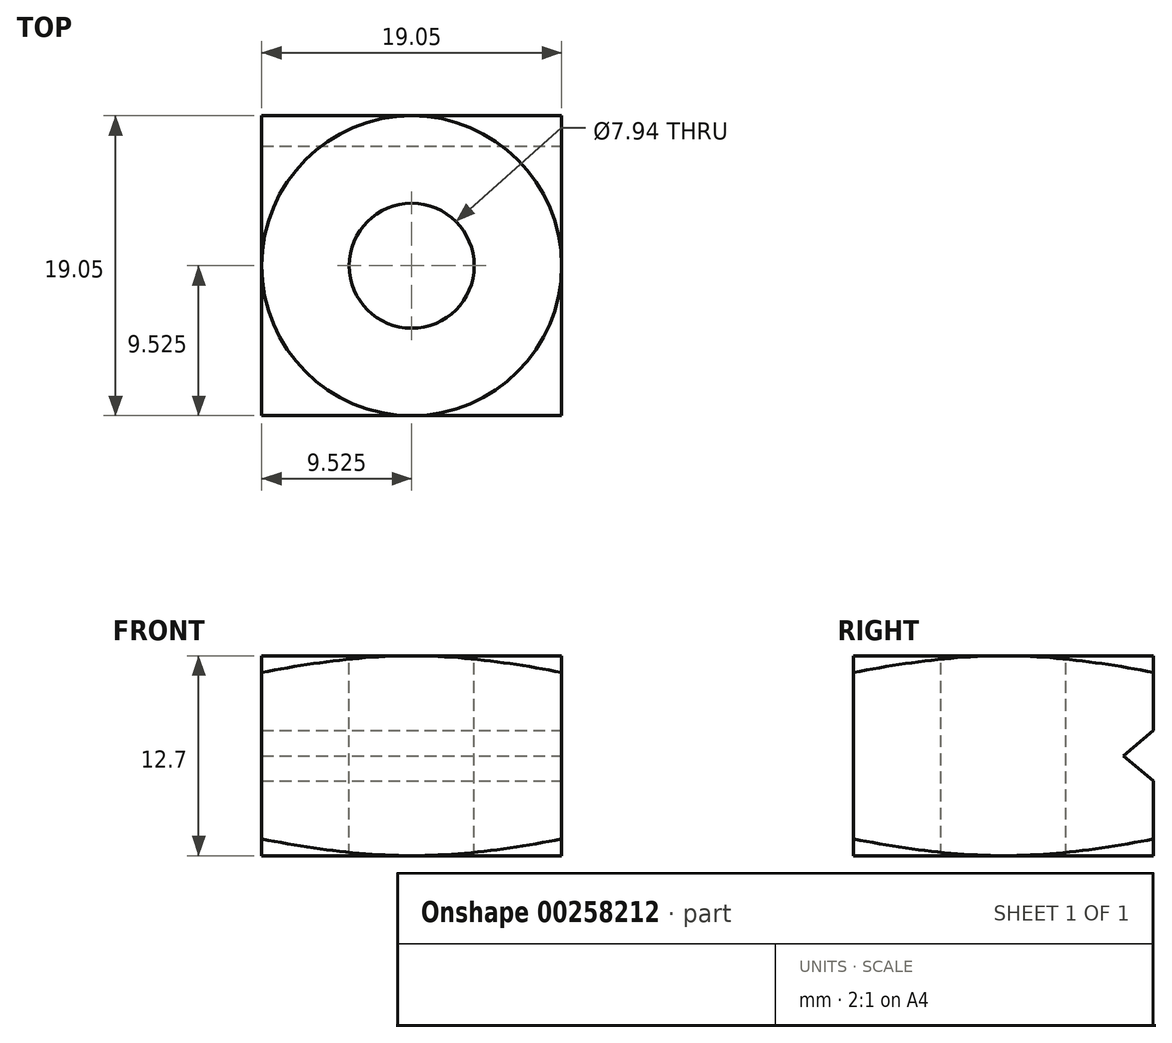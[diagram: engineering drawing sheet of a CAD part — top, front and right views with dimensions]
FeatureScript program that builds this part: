
annotation { "Feature Type Name" : "Feature", "Feature Type Description" : "" }
export const myFeature = defineFeature(function(context is Context, id is Id, definition is map)
    precondition{}
    {
        {
            var Q0;
            Q0=qCreatedBy(makeId("Top.planeOp"),FACE);
            var sketch = newSketch(context, id + "F0", { "sketchPlane" : qUnion([Q0])});
            skLineSegment(sketch, "E0.bottom", {"start": v(0, 0) * mm, "end": v(19.05, 0) * mm});
            skLineSegment(sketch, "E0.top", {"start": v(0, 19.05) * mm, "end": v(19.05, 19.05) * mm});
            skLineSegment(sketch, "E0.left", {"start": v(0, 0) * mm, "end": v(0, 19.05) * mm});
            skLineSegment(sketch, "E0.right", {"start": v(19.05, 0) * mm, "end": v(19.05, 19.05) * mm});
            skSolve(sketch);
        }
        {
            var Q0;
            Q0 = qSketchRegion(id + "F0", true);
            extrude(context, id + "F1", {"entities" : qUnion([Q0]), "depth" : 6.35 * mm});
        }
        {
            var Q0;
            Q0=makeQuery(id+"F1.opExtrude","CAP_FACE",FACE,{"disambiguationData":[OSD([sQuery(id+"F0.wireOp",EDGE,"E0.bottom"),sQuery(id+"F0.wireOp",EDGE,"E0.top"),sQuery(id+"F0.wireOp",EDGE,"E0.left"),sQuery(id+"F0.wireOp",EDGE,"E0.right")])],"isStart":false});
            var sketch = newSketch(context, id + "F2", { "sketchPlane" : qUnion([Q0])});
            skCircle(sketch, "E1", {"center": v(9.53, 9.53) * mm, "radius": 3.97 * mm});
            skSolve(sketch);
        }
        {
            var Q0;
            Q0 = qSketchRegion(id + "F2", true);
            extrude(context, id + "F3", {"entities" : qUnion([Q0]), "operationType" : NewBodyOperationType.REMOVE, "oppositeDirection" : true, "depth" : 12.7 * mm});
        }
        {
            var Q0;
            Q0=makeQuery(id+"F1.opExtrude","CAP_FACE",FACE,{"disambiguationData":[OSD([sQuery(id+"F0.wireOp",EDGE,"E0.bottom"),sQuery(id+"F0.wireOp",EDGE,"E0.top"),sQuery(id+"F0.wireOp",EDGE,"E0.left"),sQuery(id+"F0.wireOp",EDGE,"E0.right")])],"isStart":false});
            var sketch = newSketch(context, id + "F4", { "sketchPlane" : qUnion([Q0])});
            skCircle(sketch, "E2", {"center": v(9.53, 9.53) * mm, "radius": 9.52 * mm});
            skSolve(sketch);
        }
        {
            var Q0;
            Q0=makeQuery(id+"F1.opExtrude","SWEPT_FACE",FACE,{"disambiguationData":[OSD([sQuery(id+"F0.wireOp",EDGE,"E0.right")])]});
            var sketch = newSketch(context, id + "F5", { "sketchPlane" : qUnion([Q0])});
            skLineSegment(sketch, "E3", {"start": v(19.05, 0) * mm, "end": v(17.12, 0) * mm});
            skLineSegment(sketch, "E4", {"start": v(19.05, 0) * mm, "end": v(19.05, 1.6) * mm});
            skLineSegment(sketch, "E5", {"start": v(19.05, 1.6) * mm, "end": v(17.12, 0) * mm});
            skSolve(sketch);
        }
        {
            var Q0;
            Q0 = qSketchRegion(id + "F5", true);
            extrude(context, id + "F6", {"entities" : qUnion([Q0]), "operationType" : NewBodyOperationType.REMOVE, "oppositeDirection" : true, "depth" : 19.05 * mm});
        }
        {
            var Q0;
            Q0=makeQuery(id+"F1.opExtrude","SWEPT_FACE",FACE,{"disambiguationData":[OSD([sQuery(id+"F0.wireOp",EDGE,"E0.left")])]});
            var Q1;
            Q1=makeQuery(id+"F1.opExtrude","SWEPT_FACE",FACE,{"disambiguationData":[OSD([sQuery(id+"F0.wireOp",EDGE,"E0.right")])]});
            cPlane(context, id + "F7", {"entities" : qUnion([Q0, Q1]), "cplaneType" : CPlaneType.MID_PLANE, "offset" : 25.4 * mm, "width" : 152.4 * mm, "height" : 152.4 * mm});
        }
        {
            var Q0;
            Q0=qCreatedBy(id+"F7.planeOp",FACE);
            var sketch = newSketch(context, id + "F8", { "sketchPlane" : qUnion([Q0])});
            skLineSegment(sketch, "E6.0.0", {"start": v(-17.12, 0) * mm, "end": v(-19.05, 1.6) * mm});
            skLineSegment(sketch, "E6.0.1", {"start": v(-19.05, 1.6) * mm, "end": v(-19.05, 6.35) * mm});
            skLineSegment(sketch, "E6.0.2", {"start": v(-19.05, 6.35) * mm, "end": v(0, 6.35) * mm});
            skLineSegment(sketch, "E6.0.3", {"start": v(0, 6.35) * mm, "end": v(0, 0) * mm});
            skLineSegment(sketch, "E6.0.4", {"start": v(0, 0) * mm, "end": v(-17.12, 0) * mm});
            skLineSegment(sketch, "E7", {"start": v(-19.05, 6.35) * mm, "end": v(-28.45, 6.35) * mm});
            skLineSegment(sketch, "E8", {"start": v(-28.45, 6.35) * mm, "end": v(-28.45, 3.83) * mm});
            skLineSegment(sketch, "E9", {"start": v(-28.45, 3.83) * mm, "end": v(-19.05, 6.35) * mm});
            skSolve(sketch);
        }
        {
            var Q0;
            Q0=makeQuery(id+"F8.imprint","IMPRINT",FACE,{"disambiguationData":[TD([[makeQuery(id+"F8.imprint","IMPRINT",EDGE,{"derivedFrom":sQuery(id+"F8.wireOp",EDGE,"E7")}),1.0]])]});
            var Q1;
            Q1=sQuery(id+"F4.wireOp",EDGE,"E2");
            sweep(context, id + "F9", {"operationType" : NewBodyOperationType.REMOVE, "profiles" : qUnion([Q0]), "path" : qUnion([Q1])});
        }
        {
            var Q0;
            Q0=makeQuery(id+"F1.opExtrude","SWEPT_BODY",BODY,{"disambiguationData":[OSD([sQuery(id+"F0.wireOp",EDGE,"E0.bottom"),sQuery(id+"F0.wireOp",EDGE,"E0.top"),sQuery(id+"F0.wireOp",EDGE,"E0.left"),sQuery(id+"F0.wireOp",EDGE,"E0.right")])]});
            var Q1;
            Q1=makeQuery(id+"F1.opExtrude","CAP_FACE",FACE,{"disambiguationData":[OSD([sQuery(id+"F0.wireOp",EDGE,"E0.bottom"),sQuery(id+"F0.wireOp",EDGE,"E0.top"),sQuery(id+"F0.wireOp",EDGE,"E0.left"),sQuery(id+"F0.wireOp",EDGE,"E0.right")])],"isStart":true});
            mirror(context, id + "F10", {"operationType" : NewBodyOperationType.ADD, "entities" : qUnion([Q0]), "mirrorPlane" : qUnion([Q1])});
        }
    });
